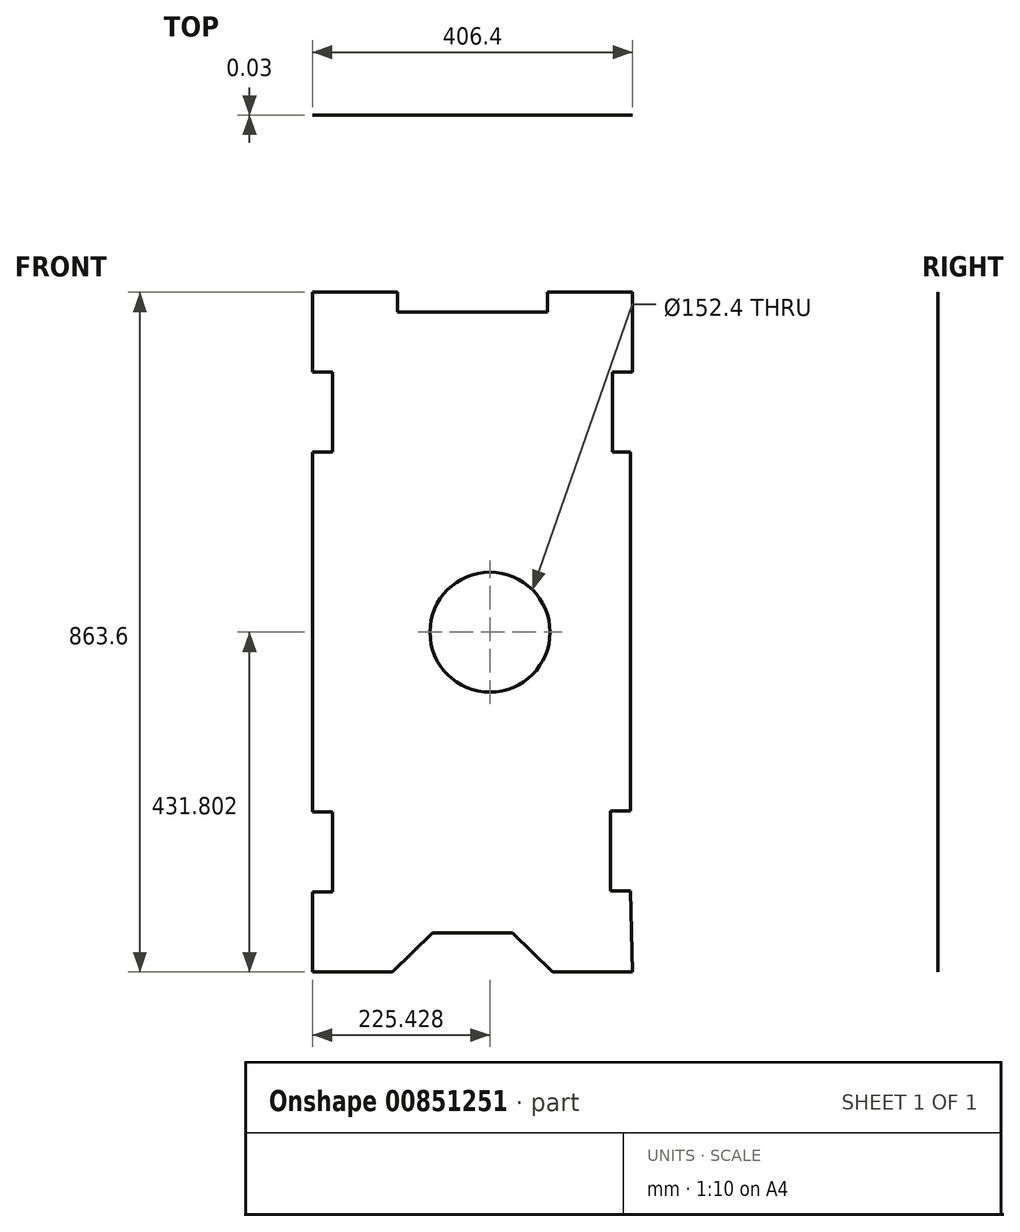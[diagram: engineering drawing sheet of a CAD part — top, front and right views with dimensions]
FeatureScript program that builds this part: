
annotation { "Feature Type Name" : "Feature", "Feature Type Description" : "" }
export const myFeature = defineFeature(function(context is Context, id is Id, definition is map)
    precondition{}
    {
        {
            var Q0;
            Q0=qCreatedBy(makeId("Front.planeOp"),FACE);
            var sketch = newSketch(context, id + "F0", { "sketchPlane" : qUnion([Q0])});
            skLineSegment(sketch, "E0", {"start": v(-277.43, -76.32) * mm, "end": v(-175.83, -76.32) * mm});
            skLineSegment(sketch, "E1", {"start": v(128.97, -76.32) * mm, "end": v(27.37, -76.32) * mm});
            skLineSegment(sketch, "E2", {"start": v(-125.03, -26.44) * mm, "end": v(-23.43, -26.44) * mm});
            skLineSegment(sketch, "E3", {"start": v(-175.83, -76.32) * mm, "end": v(-125.03, -26.44) * mm});
            skLineSegment(sketch, "E4", {"start": v(27.37, -76.32) * mm, "end": v(-23.43, -26.44) * mm});
            skLineSegment(sketch, "E5", {"start": v(128.97, 685.68) * mm, "end": v(103.57, 685.68) * mm});
            skLineSegment(sketch, "E6", {"start": v(103.57, 584.08) * mm, "end": v(103.57, 685.68) * mm});
            skLineSegment(sketch, "E7", {"start": v(103.57, 584.08) * mm, "end": v(126.4, 584.08) * mm});
            skLineSegment(sketch, "E8", {"start": v(128.97, 685.68) * mm, "end": v(128.97, 787.28) * mm});
            skLineSegment(sketch, "E9", {"start": v(126.4, 584.08) * mm, "end": v(126.4, 128.13) * mm});
            skLineSegment(sketch, "E10", {"start": v(126.4, 128.13) * mm, "end": v(101, 128.13) * mm});
            skLineSegment(sketch, "E11", {"start": v(101, 128.13) * mm, "end": v(101, 26.53) * mm});
            skLineSegment(sketch, "E12", {"start": v(101, 26.53) * mm, "end": v(126.4, 26.53) * mm});
            skLineSegment(sketch, "E13", {"start": v(126.4, 26.53) * mm, "end": v(128.97, -76.32) * mm});
            skLineSegment(sketch, "E14", {"start": v(-277.43, 685.68) * mm, "end": v(-252.03, 685.68) * mm});
            skLineSegment(sketch, "E15", {"start": v(-252.03, 685.68) * mm, "end": v(-252.03, 584.08) * mm});
            skLineSegment(sketch, "E16", {"start": v(-277.43, 584.08) * mm, "end": v(-252.03, 584.08) * mm});
            skLineSegment(sketch, "E17", {"start": v(-277.43, -76.32) * mm, "end": v(-277.43, 25.28) * mm});
            skLineSegment(sketch, "E18", {"start": v(-277.43, 25.28) * mm, "end": v(-252.03, 25.28) * mm});
            skLineSegment(sketch, "E19", {"start": v(-252.03, 25.28) * mm, "end": v(-252.03, 126.88) * mm});
            skLineSegment(sketch, "E20", {"start": v(-252.03, 126.88) * mm, "end": v(-277.43, 126.88) * mm});
            skLineSegment(sketch, "E21", {"start": v(-277.43, 787.28) * mm, "end": v(-277.43, 685.68) * mm});
            skLineSegment(sketch, "E22", {"start": v(-277.43, 584.08) * mm, "end": v(-277.43, 126.88) * mm});
            skLineSegment(sketch, "E23", {"start": v(21.02, 787.28) * mm, "end": v(21.02, 761.88) * mm});
            skCircle(sketch, "E24", {"center": v(-52, 355.48) * mm, "radius": 76.2 * mm});
            skPoint(sketch, "E24.centerSnap0", {"position": v(-277.43, 355.48) * mm});
            skLineSegment(sketch, "E25", {"start": v(128.97, 787.28) * mm, "end": v(21.02, 787.28) * mm});
            skLineSegment(sketch, "E26", {"start": v(-277.43, 787.28) * mm, "end": v(-169.48, 787.28) * mm});
            skLineSegment(sketch, "E27", {"start": v(-169.48, 787.28) * mm, "end": v(-169.48, 761.88) * mm});
            skLineSegment(sketch, "E28", {"start": v(21.02, 761.88) * mm, "end": v(-169.48, 761.88) * mm});
            skSolve(sketch);
        }
        {
            var Q0;
            Q0=makeQuery(id+"F0.imprint","IMPRINT",FACE,{"disambiguationData":[TD([[makeQuery(id+"F0.imprint","IMPRINT",EDGE,{"derivedFrom":sQuery(id+"F0.wireOp",EDGE,"E0")}),1.0]])]});
            var Q1;
            Q1=makeQuery(id+"F0.imprint","IMPRINT",FACE,{"disambiguationData":[TD([[makeQuery(id+"F0.imprint","IMPRINT",EDGE,{"derivedFrom":sQuery(id+"F0.wireOp",EDGE,"Y5CuhmuK-wucb-1bgR-0G3T-rC395NvoFyxl.bottom")}),-1.0]])]});
            var Q2;
            Q2=makeQuery(id+"F0.imprint","IMPRINT",FACE,{"disambiguationData":[TD([[makeQuery(id+"F0.imprint","IMPRINT",EDGE,{"derivedFrom":sQuery(id+"F0.wireOp",EDGE,"0285ce21-0ccf-4ba4-a15e-c29fd65026c8.bottom")}),-1.0]])]});
            var Q3;
            Q3=makeQuery(id+"F0.imprint","IMPRINT",FACE,{"disambiguationData":[TD([[makeQuery(id+"F0.imprint","IMPRINT",EDGE,{"derivedFrom":sQuery(id+"F0.wireOp",EDGE,"2s6vJXLW-tTbs-rrmN-YTcj-1ZVtnbzkIVIv")}),1.0]])]});
            extrude(context, id + "F1", {"entities" : qUnion([Q0, Q1, Q2, Q3]), "depth" : 3 / 101.6 * mm, "offsetDistance" : 25.4 * mm});
        }
    });
